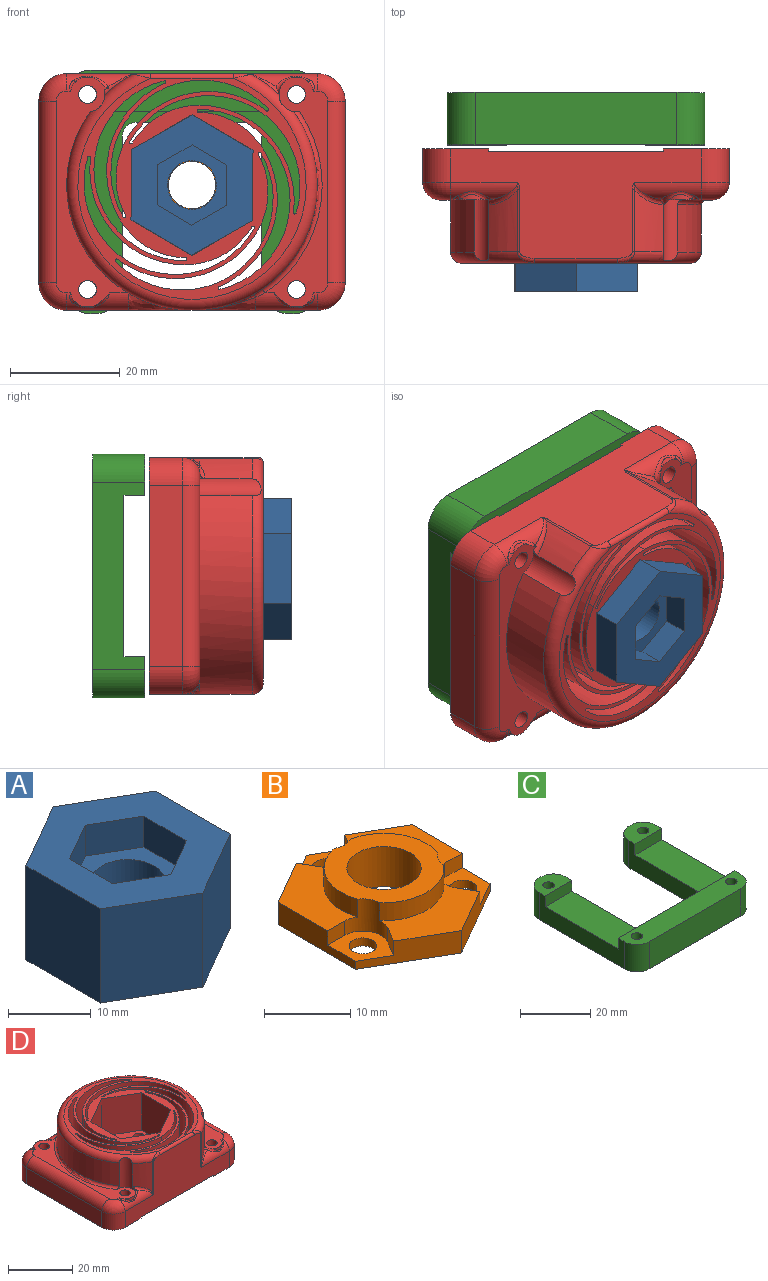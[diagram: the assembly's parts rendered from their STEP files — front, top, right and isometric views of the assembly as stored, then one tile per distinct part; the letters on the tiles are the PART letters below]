
ASSEMBLY  parts=4 mates=4
PART A: 22 faces, bbox 22.2x25.6x14 mm
  f0: cylinder r=4.45mm len=8.89mm, axis (0,0,-1), area 120.6mm2, adj f18,f21
  f1: plane 25.6x22.17mm, normal (0,0,1), area 286.1mm2, adj f2,f3,f4,f5,f6,f7,f12,f13
  f2: plane 13.97x12.8mm, normal (1,0,0), area 178.8mm2, adj f1,f3,f7,f8
  f3: plane 13.97x11.09mm, normal (0.5,0.87,0), area 178.8mm2, adj f1,f2,f4,f8
  f4: plane 13.97x11.09mm, normal (-0.5,0.87,0), area 178.8mm2, adj f1,f3,f5,f8
  f5: plane 13.97x12.8mm, normal (-1,0,0), area 178.8mm2, adj f1,f4,f6,f8
  f6: plane 13.97x11.09mm, normal (-0.5,-0.87,0), area 178.8mm2, adj f1,f5,f7,f8
  f7: plane 13.97x11.09mm, normal (0.5,-0.87,0), area 178.8mm2, adj f1,f2,f6,f8
  f8: plane 25.6x22.17mm, normal (0,0,-1), area 140.8mm2, adj f2,f3,f4,f5,f6,f7,f10
  f9: cylinder r=6.99mm len=13.97mm, axis (0,0,-1), area 89.2mm2, adj f19,f21
  f10: cylinder r=9.53mm len=19.05mm, axis (0,0,-1), area 425.6mm2, adj f8,f20
  f11: plane 17.53x17.53mm, normal (0,0,-1), area 52.7mm2, adj f19,f20
  f12: plane 7.33x4.57mm, normal (1,0,0), area 33.5mm2, adj f1,f13,f17,f18
  f13: plane 6.35x4.57mm, normal (0.5,0.87,0), area 33.5mm2, adj f1,f12,f14,f18
  f14: plane 6.35x4.57mm, normal (-0.5,0.87,0), area 33.5mm2, adj f1,f13,f15,f18
  f15: plane 7.33x4.57mm, normal (-1,0,0), area 33.5mm2, adj f1,f14,f16,f18
  f16: plane 6.35x4.57mm, normal (-0.5,-0.87,0), area 33.5mm2, adj f1,f15,f17,f18
  f17: plane 6.35x4.57mm, normal (0.5,-0.87,0), area 33.5mm2, adj f1,f12,f16,f18
  f18: plane 14.66x12.7mm, normal (0,0,1), area 77.6mm2, adj f0,f12,f13,f14,f15,f16,f17
  f19: torus R=7.75mm, axis (0,0,-1), area 54.6mm2, adj f9,f11
  f20: torus R=8.76mm, axis (0,0,-1), area 69.6mm2, adj f10,f11
  f21: plane 13.97x13.97mm, normal (0,0,-1), area 91.2mm2, adj f0,f9
PART B: 30 faces, bbox 22.1x25.5x5.7 mm
  f0: plane 12.73x9.71mm, normal (0,0,1), area 60.1mm2, adj f4,f5,f15,f16,f22,f24,f28
  f1: plane 12.73x9.71mm, normal (0,0,1), area 60.1mm2, adj f2,f3,f14,f16,f19,f20,f27
  f2: plane 12.76x3.18mm, normal (1,0,0), area 31.2mm2, adj f1,f3,f7,f13,f19,f21
  f3: plane 11.05x6.38mm, normal (0.5,0.87,0), area 31.2mm2, adj f1,f2,f4,f13,f14,f17
  f4: plane 11.05x6.38mm, normal (-0.5,0.87,0), area 31.2mm2, adj f0,f3,f5,f13,f15,f17
  f5: plane 12.76x3.18mm, normal (-1,0,0), area 31.2mm2, adj f0,f4,f6,f13,f22,f25
  f6: plane 11.05x6.38mm, normal (-0.5,-0.87,0), area 31.2mm2, adj f5,f7,f11,f13,f23,f25
  f7: plane 11.05x6.38mm, normal (0.5,-0.87,0), area 31.2mm2, adj f2,f6,f11,f13,f18,f21
  f8: cylinder r=1.59mm len=3.18mm, axis (0,0,-1), area 11.4mm2, adj f13,f17
  f9: cylinder r=1.59mm len=3.18mm, axis (0,0,-1), area 11.4mm2, adj f13,f21
  f10: cylinder r=1.59mm len=3.18mm, axis (0,0,-1), area 11.4mm2, adj f13,f25
  f11: plane 14.13x8.17mm, normal (0,0,1), area 60.1mm2, adj f6,f7,f18,f20,f23,f24,f26
  f12: cylinder r=4.32mm len=8.64mm, axis (0,0,-1), area 155.1mm2, adj f13,f29
  f13: plane 25.52x22.1mm, normal (0,0,-1), area 340.6mm2, adj f2,f3,f4,f5,f6,f7,f8,f9
  f14: plane 2.43x2.03mm, normal (-0.87,0.5,0), area 5.7mm2, adj f1,f3,f16,f17
  f15: plane 2.43x2.03mm, normal (0.87,0.5,0), area 5.7mm2, adj f0,f4,f16,f17
  f16: cylinder r=2.98mm len=5.17mm, axis (0,0,1), area 19.7mm2, adj f0,f1,f14,f15,f17,f27,f28,f29
  f17: plane 7.97x6.22mm, normal (0,0,1), area 22.7mm2, adj f3,f4,f8,f14,f15,f16
  f18: plane 2.43x2.03mm, normal (0.87,0.5,0), area 5.7mm2, adj f7,f11,f20,f21
  f19: plane 2.8x2.03mm, normal (0,-1,0), area 5.7mm2, adj f1,f2,f20,f21
  f20: cylinder r=2.98mm len=4.57mm, axis (0,0,1), area 19.7mm2, adj f1,f11,f18,f19,f21,f26,f27,f29
  f21: plane 6.9x5.78mm, normal (0,0,1), area 22.7mm2, adj f2,f7,f9,f18,f19,f20
  f22: plane 2.8x2.03mm, normal (0,-1,0), area 5.7mm2, adj f0,f5,f24,f25
  f23: plane 2.43x2.03mm, normal (-0.87,0.5,0), area 5.7mm2, adj f6,f11,f24,f25
  f24: cylinder r=2.98mm len=4.57mm, axis (0,0,1), area 19.7mm2, adj f0,f11,f22,f23,f25,f26,f28,f29
  f25: plane 6.9x5.78mm, normal (0,0,1), area 22.7mm2, adj f5,f6,f10,f22,f23,f24
  f26: cylinder r=6.99mm len=10.54mm, axis (0,0,-1), area 30.3mm2, adj f11,f20,f24,f29
  f27: cylinder r=6.99mm len=9.13mm, axis (0,0,-1), area 30.3mm2, adj f1,f16,f20,f29
  f28: cylinder r=6.99mm len=9.13mm, axis (0,0,-1), area 30.3mm2, adj f0,f16,f24,f29
  f29: plane 13.97x13.84mm, normal (0,0,1), area 92.3mm2, adj f12,f16,f20,f24,f26,f27,f28
PART C: 56 faces, bbox 47x44.5x9.5 mm
  f0: cylinder r=1.63mm len=5.46mm, axis (0,0,-1), area 55.8mm2, adj f23,f34
  f1: cylinder r=1.63mm len=5.46mm, axis (0,0,-1), area 55.8mm2, adj f9,f41
  f2: cylinder r=1.63mm len=5.46mm, axis (0,0,-1), area 55.8mm2, adj f10,f48
  f3: cylinder r=1.63mm len=5.46mm, axis (0,0,-1), area 55.8mm2, adj f10,f55
  f4: plane 46.99x44.45mm, normal (0,0,-1), area 1066.9mm2, adj f5,f6,f7,f8,f11,f12,f13,f14
  f5: plane 34.29x9.53mm, normal (1,0,0), area 214.4mm2, adj f4,f9,f10,f12,f13,f24,f25,f27
  f6: cylinder r=2.54mm len=5.72mm, axis (0,0,-1), area 22.8mm2, adj f4,f7,f16,f24
  f7: plane 20.32x5.72mm, normal (0,1,0), area 116.1mm2, adj f4,f6,f8,f24
  f8: cylinder r=2.54mm len=5.72mm, axis (0,0,-1), area 22.8mm2, adj f4,f7,f17,f24
  f9: plane 10.8x7.49mm, normal (0,0,1), area 61.5mm2, adj f1,f5,f13,f14,f15,f16,f25
  f10: plane 46.99x7.49mm, normal (0,0,1), area 324.4mm2, adj f2,f3,f5,f11,f12,f21,f22,f27
  f11: plane 36.83x9.53mm, normal (0,-1,0), area 350.8mm2, adj f4,f10,f12,f22
  f12: cylinder r=5.08mm len=9.53mm, axis (0,0,-1), area 76mm2, adj f4,f5,f10,f11
  f13: cylinder r=5.08mm len=9.53mm, axis (0,0,-1), area 76mm2, adj f4,f5,f9,f14
  f14: plane 9.53x0.64mm, normal (0,1,0), area 6mm2, adj f4,f9,f13,f15
  f15: cylinder r=5.08mm len=9.53mm, axis (0,0,-1), area 76mm2, adj f4,f9,f14,f16
  f16: plane 27.31x9.53mm, normal (-1,0,0), area 165.2mm2, adj f4,f6,f9,f15,f24,f25
  f17: plane 27.31x9.53mm, normal (1,0,0), area 165.2mm2, adj f4,f8,f18,f23,f24,f26
  f18: cylinder r=5.08mm len=9.53mm, axis (0,0,-1), area 76mm2, adj f4,f17,f19,f23
  f19: plane 9.53x0.64mm, normal (0,1,0), area 6mm2, adj f4,f18,f20,f23
  f20: cylinder r=5.08mm len=9.53mm, axis (0,0,-1), area 76mm2, adj f4,f19,f21,f23
  f21: plane 34.29x9.53mm, normal (-1,0,0), area 214.4mm2, adj f4,f10,f20,f22,f23,f24,f26,f27
  f22: cylinder r=5.08mm len=9.53mm, axis (0,0,-1), area 76mm2, adj f4,f10,f11,f21
  f23: plane 10.8x7.49mm, normal (0,0,1), area 61.5mm2, adj f0,f17,f18,f19,f20,f21,f26
  f24: plane 46.99x29.46mm, normal (0,0,1), area 690.5mm2, adj f5,f6,f7,f8,f16,f17,f21,f25
  f25: plane 10.8x3.81mm, normal (0,-1,0), area 41.1mm2, adj f5,f9,f16,f24
  f26: plane 10.8x3.81mm, normal (0,-1,0), area 41.1mm2, adj f17,f21,f23,f24
  f27: plane 46.99x3.81mm, normal (0,1,0), area 179mm2, adj f5,f10,f21,f24
  f28: plane 4.06x3.17mm, normal (0,1,0), area 12.9mm2, adj f4,f29,f33,f34
  f29: plane 4.06x2.74mm, normal (0.87,0.5,0), area 12.9mm2, adj f4,f28,f30,f34
  f30: plane 4.06x2.74mm, normal (0.87,-0.5,0), area 12.9mm2, adj f4,f29,f31,f34
  f31: plane 4.06x3.17mm, normal (0,-1,0), area 12.9mm2, adj f4,f30,f32,f34
  f32: plane 4.06x2.74mm, normal (-0.87,-0.5,0), area 12.9mm2, adj f4,f31,f33,f34
  f33: plane 4.06x2.74mm, normal (-0.87,0.5,0), area 12.9mm2, adj f4,f28,f32,f34
  f34: plane 6.34x5.49mm, normal (0,0,-1), area 17.8mm2, adj f0,f28,f29,f30,f31,f32,f33
  f35: plane 4.06x2.74mm, normal (0.87,0.5,0), area 12.9mm2, adj f4,f36,f40,f41
  f36: plane 4.06x2.74mm, normal (0.87,-0.5,0), area 12.9mm2, adj f4,f35,f37,f41
  f37: plane 4.06x3.17mm, normal (0,-1,0), area 12.9mm2, adj f4,f36,f38,f41
  f38: plane 4.06x2.74mm, normal (-0.87,-0.5,0), area 12.9mm2, adj f4,f37,f39,f41
  f39: plane 4.06x2.74mm, normal (-0.87,0.5,0), area 12.9mm2, adj f4,f38,f40,f41
  f40: plane 4.06x3.17mm, normal (0,1,0), area 12.9mm2, adj f4,f35,f39,f41
  f41: plane 6.34x5.49mm, normal (0,0,-1), area 17.8mm2, adj f1,f35,f36,f37,f38,f39,f40
  f42: plane 4.06x2.74mm, normal (0.87,-0.5,0), area 12.9mm2, adj f4,f43,f47,f48
  f43: plane 4.06x3.17mm, normal (0,-1,0), area 12.9mm2, adj f4,f42,f44,f48
  f44: plane 4.06x2.74mm, normal (-0.87,-0.5,0), area 12.9mm2, adj f4,f43,f45,f48
  f45: plane 4.06x2.74mm, normal (-0.87,0.5,0), area 12.9mm2, adj f4,f44,f46,f48
  f46: plane 4.06x3.17mm, normal (0,1,0), area 12.9mm2, adj f4,f45,f47,f48
  f47: plane 4.06x2.74mm, normal (0.87,0.5,0), area 12.9mm2, adj f4,f42,f46,f48
  f48: plane 6.34x5.49mm, normal (0,0,-1), area 17.8mm2, adj f2,f42,f43,f44,f45,f46,f47
  f49: plane 4.06x2.74mm, normal (0.87,-0.5,0), area 12.9mm2, adj f4,f50,f54,f55
  f50: plane 4.06x3.17mm, normal (0,-1,0), area 12.9mm2, adj f4,f49,f51,f55
  f51: plane 4.06x2.74mm, normal (-0.87,-0.5,0), area 12.9mm2, adj f4,f50,f52,f55
  f52: plane 4.06x2.74mm, normal (-0.87,0.5,0), area 12.9mm2, adj f4,f51,f53,f55
  f53: plane 4.06x3.17mm, normal (0,1,0), area 12.9mm2, adj f4,f52,f54,f55
  f54: plane 4.06x2.74mm, normal (0.87,0.5,0), area 12.9mm2, adj f4,f49,f53,f55
  f55: plane 6.34x5.49mm, normal (0,0,-1), area 17.8mm2, adj f3,f49,f50,f51,f52,f53,f54
PART D: 136 faces, bbox 56.4x48.4x21.6 mm
  f0: plane 33.02x6.1mm, normal (1,0,0), area 201.3mm2, adj f8,f10,f90,f106
  f1: plane 33.02x6.1mm, normal (-1,0,0), area 201.3mm2, adj f7,f9,f94,f101
  f2: plane 45.72x19.94mm, normal (0,-1,0), area 545.6mm2, adj f9,f10,f14,f87,f90,f91,f94,f103
  f3: plane 41.66x40.26mm, normal (0,0,1), area 487.1mm2, adj f16,f17,f18,f19,f20,f21,f22,f23
  f4: plane 46.29x9.84mm, normal (0,1,0), area 290.7mm2, adj f7,f8,f14,f89,f90,f92,f94,f98
  f5: cylinder r=3.17mm len=11.16mm, axis (0,0,1), area 49.9mm2, adj f82,f96,f97,f110,f111,f112,f125
  f6: cylinder r=3.17mm len=11.16mm, axis (0,0,1), area 48.2mm2, adj f85,f95,f96,f110,f115
  f7: cylinder r=5.08mm len=6.1mm, axis (0,0,-1), area 48.6mm2, adj f1,f4,f94,f100
  f8: cylinder r=5.08mm len=6.1mm, axis (0,0,1), area 48.6mm2, adj f0,f4,f90,f107
  f9: cylinder r=5.08mm len=6.1mm, axis (0,0,1), area 48.6mm2, adj f1,f2,f94,f102
  f10: cylinder r=5.08mm len=6.1mm, axis (0,0,-1), area 48.6mm2, adj f0,f2,f90,f105
  f11: cylinder r=1.62mm len=3.25mm, axis (0,0,-1), area 20.7mm2, adj f47,f67
  f12: cylinder r=1.62mm len=3.25mm, axis (0,0,-1), area 20.7mm2, adj f47,f74
  f13: cylinder r=1.62mm len=3.25mm, axis (0,0,-1), area 20.7mm2, adj f47,f60
  f14: plane 44.45x43.18mm, normal (0,0,-1), area 1072.3mm2, adj f2,f4,f15,f16,f17,f18,f19,f20
  f15: cylinder r=4.32mm len=8.64mm, axis (0,0,-1), area 68.9mm2, adj f14,f46
  f16: cylinder r=17.39mm len=24.71mm, axis (0,0,-1), area 598.9mm2, adj f3,f14,f17,f45
  f17: cylinder r=14.21mm len=20.32mm, axis (0,0,-1), area 297.5mm2, adj f3,f14,f16,f18
  f18: cylinder r=0.25mm len=20.32mm, axis (0,0,-1), area 16.1mm2, adj f3,f14,f17,f19
  f19: cylinder r=16.63mm len=32.81mm, axis (0,0,-1), area 984.6mm2, adj f3,f14,f18,f45
  f20: cylinder r=0.25mm len=20.32mm, axis (0,0,-1), area 15.4mm2, adj f3,f14,f21,f40
  f21: cylinder r=17.39mm len=25.55mm, axis (0,0,-1), area 598.9mm2, adj f3,f14,f20,f22
  f22: cylinder r=14.21mm len=20.32mm, axis (0,0,-1), area 297.5mm2, adj f3,f14,f21,f23
  f23: cylinder r=0.25mm len=20.32mm, axis (0,0,-1), area 16.1mm2, adj f3,f14,f22,f40
  f24: cylinder r=0.25mm len=20.32mm, axis (0,0,-1), area 15.4mm2, adj f3,f14,f25,f41
  f25: cylinder r=17.39mm len=20.32mm, axis (0,0,-1), area 598.9mm2, adj f3,f14,f24,f26
  f26: cylinder r=14.21mm len=20.32mm, axis (0,0,-1), area 297.5mm2, adj f3,f14,f25,f27
  f27: cylinder r=0.25mm len=20.32mm, axis (0,0,-1), area 16.1mm2, adj f3,f14,f26,f41
  f28: cylinder r=0.25mm len=20.32mm, axis (0,0,-1), area 15.4mm2, adj f3,f14,f29,f42
  f29: cylinder r=17.39mm len=24.71mm, axis (0,0,-1), area 598.9mm2, adj f3,f14,f28,f30
  f30: cylinder r=14.21mm len=20.32mm, axis (0,0,-1), area 297.5mm2, adj f3,f14,f29,f31
  f31: cylinder r=0.25mm len=20.32mm, axis (0,0,-1), area 16.1mm2, adj f3,f14,f30,f42
  f32: cylinder r=0.25mm len=20.32mm, axis (0,0,-1), area 15.4mm2, adj f3,f14,f33,f43
  f33: cylinder r=17.39mm len=25.55mm, axis (0,0,-1), area 598.9mm2, adj f3,f14,f32,f34
  f34: cylinder r=14.21mm len=20.32mm, axis (0,0,-1), area 297.5mm2, adj f3,f14,f33,f35
  f35: cylinder r=0.25mm len=20.32mm, axis (0,0,-1), area 16.1mm2, adj f3,f14,f34,f43
  f36: cylinder r=0.25mm len=20.32mm, axis (0,0,-1), area 15.4mm2, adj f3,f14,f37,f44
  f37: cylinder r=17.39mm len=20.32mm, axis (0,0,-1), area 598.9mm2, adj f3,f14,f36,f38
  f38: cylinder r=14.21mm len=20.32mm, axis (0,0,-1), area 297.5mm2, adj f3,f14,f37,f39
  f39: cylinder r=0.25mm len=20.32mm, axis (0,0,-1), area 16.1mm2, adj f3,f14,f38,f44
  f40: cylinder r=16.63mm len=28.73mm, axis (0,0,-1), area 984.6mm2, adj f3,f14,f20,f23
  f41: cylinder r=16.63mm len=31.07mm, axis (0,0,-1), area 984.6mm2, adj f3,f14,f24,f27
  f42: cylinder r=16.63mm len=32.81mm, axis (0,0,-1), area 984.6mm2, adj f3,f14,f28,f31
  f43: cylinder r=16.63mm len=28.73mm, axis (0,0,-1), area 984.6mm2, adj f3,f14,f32,f35
  f44: cylinder r=16.63mm len=31.07mm, axis (0,0,-1), area 984.6mm2, adj f3,f14,f36,f39
  f45: cylinder r=0.25mm len=20.32mm, axis (0,0,-1), area 15.4mm2, adj f3,f14,f16,f19
  f46: plane 14.81x12.83mm, normal (0,0,1), area 83.9mm2, adj f15,f48,f49,f50,f51,f52,f53
  f47: plane 25.66x22.23mm, normal (0,0,1), area 260.4mm2, adj f11,f12,f13,f48,f49,f50,f51,f52
  f48: plane 7.41x3.56mm, normal (0,-1,0), area 26.3mm2, adj f46,f47,f49,f53
  f49: plane 6.41x3.7mm, normal (0.87,-0.5,0), area 26.3mm2, adj f46,f47,f48,f50
  f50: plane 6.41x3.7mm, normal (0.87,0.5,0), area 26.3mm2, adj f46,f47,f49,f51
  f51: plane 7.41x3.56mm, normal (0,1,0), area 26.3mm2, adj f46,f47,f50,f52
  f52: plane 6.41x3.7mm, normal (-0.87,0.5,0), area 26.3mm2, adj f46,f47,f51,f53
  f53: plane 6.41x3.7mm, normal (-0.87,-0.5,0), area 26.3mm2, adj f46,f47,f48,f52
  f54: plane 4.06x2.74mm, normal (0.87,0.5,0), area 12.9mm2, adj f14,f55,f59,f60
  f55: plane 4.06x2.74mm, normal (0.87,-0.5,0), area 12.9mm2, adj f14,f54,f56,f60
  f56: plane 4.06x3.17mm, normal (0,-1,0), area 12.9mm2, adj f14,f55,f57,f60
  f57: plane 4.06x2.74mm, normal (-0.87,-0.5,0), area 12.9mm2, adj f14,f56,f58,f60
  f58: plane 4.06x2.74mm, normal (-0.87,0.5,0), area 12.9mm2, adj f14,f57,f59,f60
  f59: plane 4.06x3.17mm, normal (0,1,0), area 12.9mm2, adj f14,f54,f58,f60
  f60: plane 6.34x5.49mm, normal (0,0,-1), area 17.8mm2, adj f13,f54,f55,f56,f57,f58,f59
  f61: plane 4.06x2.74mm, normal (0.87,0.5,0), area 12.9mm2, adj f14,f62,f66,f67
  f62: plane 4.06x2.74mm, normal (0.87,-0.5,0), area 12.9mm2, adj f14,f61,f63,f67
  f63: plane 4.06x3.17mm, normal (0,-1,0), area 12.9mm2, adj f14,f62,f64,f67
  f64: plane 4.06x2.74mm, normal (-0.87,-0.5,0), area 12.9mm2, adj f14,f63,f65,f67
  f65: plane 4.06x2.74mm, normal (-0.87,0.5,0), area 12.9mm2, adj f14,f64,f66,f67
  f66: plane 4.06x3.17mm, normal (0,1,0), area 12.9mm2, adj f14,f61,f65,f67
  f67: plane 6.34x5.49mm, normal (0,0,-1), area 17.8mm2, adj f11,f61,f62,f63,f64,f65,f66
  f68: plane 4.06x2.74mm, normal (-0.87,-0.5,0), area 12.9mm2, adj f14,f69,f73,f74
  f69: plane 4.06x2.74mm, normal (-0.87,0.5,0), area 12.9mm2, adj f14,f68,f70,f74
  f70: plane 4.06x3.17mm, normal (0,1,0), area 12.9mm2, adj f14,f69,f71,f74
  f71: plane 4.06x2.74mm, normal (0.87,0.5,0), area 12.9mm2, adj f14,f70,f72,f74
  f72: plane 4.06x2.74mm, normal (0.87,-0.5,0), area 12.9mm2, adj f14,f71,f73,f74
  f73: plane 4.06x3.17mm, normal (0,-1,0), area 12.9mm2, adj f14,f68,f72,f74
  f74: plane 6.34x5.49mm, normal (0,0,-1), area 17.8mm2, adj f12,f68,f69,f70,f71,f72,f73
  f75: plane 14.22x12.83mm, normal (1,0,0), area 182.5mm2, adj f3,f47,f76,f80
  f76: plane 14.22x11.11mm, normal (0.5,0.87,0), area 182.5mm2, adj f3,f47,f75,f77
  f77: plane 14.22x11.11mm, normal (-0.5,0.87,0), area 182.5mm2, adj f3,f47,f76,f78
  f78: plane 14.22x12.83mm, normal (-1,0,0), area 182.5mm2, adj f3,f47,f77,f79
  f79: plane 14.22x11.11mm, normal (-0.5,-0.87,0), area 182.5mm2, adj f3,f47,f78,f80
  f80: plane 14.22x11.11mm, normal (0.5,-0.87,0), area 182.5mm2, adj f3,f47,f75,f79
  f81: cylinder r=1.62mm len=9.27mm, axis (0,0,1), area 94.7mm2, adj f82,f94
  f82: plane 42.43x12mm, normal (0,0,1), area 150.2mm2, adj f5,f81,f83,f99,f100,f101,f102,f103
  f83: cylinder r=1.62mm len=9.27mm, axis (0,0,1), area 94.7mm2, adj f82,f94
  f84: cylinder r=1.62mm len=9.27mm, axis (0,0,1), area 94.7mm2, adj f85,f90
  f85: plane 42.43x13.66mm, normal (0,0,1), area 184.1mm2, adj f6,f84,f86,f96,f104,f105,f106,f107
  f86: cylinder r=1.62mm len=9.27mm, axis (0,0,1), area 94.7mm2, adj f85,f90
  f87: plane 4.77x0.51mm, normal (-1,0,0), area 2.4mm2, adj f2,f14,f88,f90
  f88: cylinder r=22.23mm len=31.11mm, axis (0,0,1), area 17.5mm2, adj f14,f87,f89,f90
  f89: plane 7.31x0.51mm, normal (-1,0,0), area 3.7mm2, adj f4,f14,f88,f90
  f90: plane 43.18x12.07mm, normal (0,0,-1), area 357.3mm2, adj f0,f2,f4,f8,f10,f84,f86,f87
  f91: plane 4.77x0.51mm, normal (1,0,0), area 2.4mm2, adj f2,f14,f93,f94
  f92: plane 7.31x0.51mm, normal (1,0,0), area 3.7mm2, adj f4,f14,f93,f94
  f93: cylinder r=22.23mm len=31.11mm, axis (0,0,1), area 17.5mm2, adj f14,f91,f92,f94
  f94: plane 43.18x12.07mm, normal (0,0,-1), area 357.3mm2, adj f1,f2,f4,f7,f9,f81,f83,f91
  f95: cylinder r=22.86mm len=11.42mm, axis (0,0,1), area 64.7mm2, adj f6,f110,f115,f130
  f96: cylinder r=22.86mm len=45.72mm, axis (0,0,1), area 917.7mm2, adj f5,f6,f85,f108,f110,f112,f113,f114
  f97: cylinder r=22.86mm len=11.42mm, axis (0,0,1), area 64.7mm2, adj f5,f110,f111,f134
  f98: bspline ~12.01x3.36mm, area 15.4mm2, adj f4,f99,f114
  f99: cylinder r=3.17mm len=11.24mm, axis (1,0,0), area 37.9mm2, adj f4,f82,f98,f100,f113,f127,f128
  f100: torus R=1.91mm, axis (0,0,1), area 30.8mm2, adj f7,f82,f99,f101
  f101: cylinder r=3.17mm len=33.02mm, axis (0,1,0), area 164.7mm2, adj f1,f82,f100,f102
  f102: torus R=1.91mm, axis (0,0,1), area 30.8mm2, adj f9,f82,f101,f103
  f103: cylinder r=3.17mm len=12.17mm, axis (-1,0,0), area 32.1mm2, adj f2,f82,f102,f111,f125,f126
  f104: cylinder r=3.17mm len=12.17mm, axis (-1,0,0), area 32.1mm2, adj f2,f85,f105,f115,f120,f121
  f105: torus R=1.91mm, axis (0,0,1), area 30.8mm2, adj f10,f85,f104,f106
  f106: cylinder r=3.17mm len=33.02mm, axis (0,-1,0), area 164.7mm2, adj f0,f85,f105,f107
  f107: torus R=1.91mm, axis (0,0,1), area 30.8mm2, adj f8,f85,f106,f109
  f108: bspline ~12.01x3.36mm, area 18.4mm2, adj f4,f96,f109
  f109: cylinder r=3.17mm len=11.24mm, axis (1,0,0), area 38.5mm2, adj f4,f85,f107,f108,f123,f124
  f110: torus R=20.83mm, axis (0,0,1), area 371mm2, adj f3,f5,f6,f95,f96,f97,f131,f133
  f111: bspline ~6.43x4.36mm, area 6.2mm2, adj f5,f97,f103,f125,f135
  f112: torus R=23.75mm, axis (0,0,1), area 51.4mm2, adj f5,f82,f96,f113
  f113: bspline ~4.69x2.85mm, area 2.4mm2, adj f96,f99,f112,f114
  f114: bspline ~11.78x3.05mm, area 4.4mm2, adj f96,f98,f113
  f115: bspline ~6.91x4.64mm, area 6.4mm2, adj f6,f85,f95,f104,f122,f129
  f116: cylinder r=3.17mm len=3.97mm, axis (0,0,1), area 0mm2, adj f82,f128
  f117: cylinder r=3.17mm len=3.97mm, axis (0,0,1), area 0mm2, adj f82,f125
  f118: cylinder r=3.17mm len=3.97mm, axis (0,0,1), area 0mm2, adj f85,f121
  f119: cylinder r=3.17mm len=3.97mm, axis (0,0,1), area 0mm2, adj f85,f123
  f120: bspline ~2.19x1.57mm, area 0.7mm2, adj f85,f104,f121
  f121: bspline ~6.6x2.61mm, area 4.7mm2, adj f85,f104,f118,f120,f122
  f122: sphere r=0.89mm, area 0mm2, adj f85,f115,f121
  f123: bspline ~6.86x3.1mm, area 4.9mm2, adj f85,f109,f119,f124
  f124: bspline ~2.19x1.57mm, area 0.7mm2, adj f85,f109,f123
  f125: bspline ~6.71x3.54mm, area 6.3mm2, adj f5,f103,f111,f117,f126
  f126: bspline ~2.19x1.57mm, area 0.7mm2, adj f82,f103,f125
  f127: bspline ~2.19x1.57mm, area 0.7mm2, adj f82,f99,f128
  f128: bspline ~6.75x3.23mm, area 4.9mm2, adj f82,f99,f116,f127
  f129: bspline ~1.28x0.43mm, area 0.2mm2, adj f2,f115,f130
  f130: cylinder r=0.89mm len=11.42mm, axis (0,0,1), area 4.9mm2, adj f2,f95,f129,f131
  f131: bspline ~4.02x2.46mm, area 3.3mm2, adj f2,f110,f130,f132
  f132: cylinder r=0.89mm len=15mm, axis (-1,0,0), area 20.9mm2, adj f2,f3,f131,f133
  f133: bspline ~4.02x2.27mm, area 3.3mm2, adj f2,f110,f132,f134
  f134: cylinder r=0.89mm len=11.42mm, axis (0,0,1), area 4.9mm2, adj f2,f97,f133,f135
  f135: bspline ~1.92x0.6mm, area 0.2mm2, adj f2,f111,f134
PLACE A rot(axis=(0.38,-0.65,0.65),138.3deg) t=(0,-11.48,0)mm
PLACE B rot(axis=(1,0.01,-0.01),90deg) t=(0,-7.32,0)mm
PLACE C rot(axis=(0,-0.71,0.71),180deg) t=(0,10.8,-1.27)mm
PLACE D rot(axis=(0,-0.71,0.71),180deg) t=(0,0,0)mm fixed
MATE cylindrical D.f15 <-> B.f12  axis (0,1,0) through (0,-1.27,0)mm
MATE cylindrical A.f0 <-> D.f15  axis (0,1,0) through (0,-16.56,0)mm
MATE planar B.f12 <-> D.f15  axis (0,1,0) through (0,-7.32,0)mm
MATE revolute C.f3 <-> D.f5  axis (0,-1,0) through (19.05,1.27,16.51)mm
